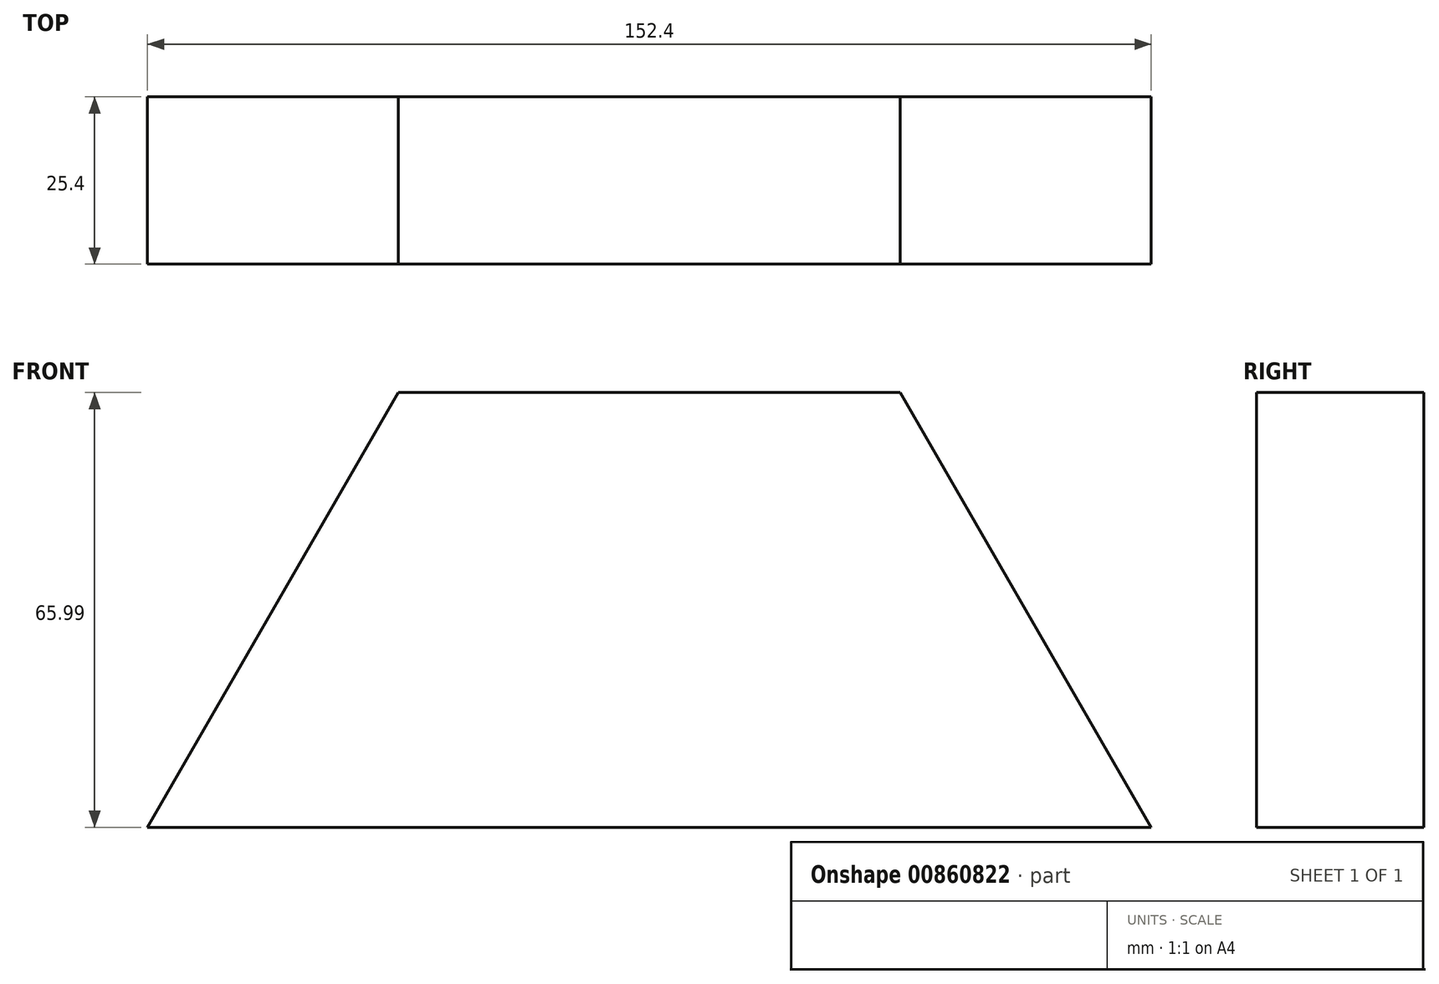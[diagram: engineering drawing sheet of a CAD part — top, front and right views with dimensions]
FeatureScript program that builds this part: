
annotation { "Feature Type Name" : "Feature", "Feature Type Description" : "" }
export const myFeature = defineFeature(function(context is Context, id is Id, definition is map)
    precondition{}
    {
        {
            var Q0;
            Q0=qCreatedBy(makeId("Front.planeOp"),FACE);
            var sketch = newSketch(context, id + "F0", { "sketchPlane" : qUnion([Q0])});
            skLineSegment(sketch, "E0", {"start": v(-49.84, -32.76) * mm, "end": v(102.56, -32.76) * mm});
            skLineSegment(sketch, "E1", {"start": v(102.56, -32.76) * mm, "end": v(64.46, 33.23) * mm});
            skLineSegment(sketch, "E2", {"start": v(64.46, 33.23) * mm, "end": v(-11.74, 33.23) * mm});
            skLineSegment(sketch, "E3", {"start": v(-11.74, 33.23) * mm, "end": v(-49.84, -32.76) * mm});
            skSolve(sketch);
        }
        {
            var Q0;
            Q0=qSketchRegion(id+"F0",true);
            extrude(context, id + "F1", {"entities" : qUnion([Q0]), "depth" : 25.4 * mm, "offsetDistance" : 25.4 * mm});
        }
    });
